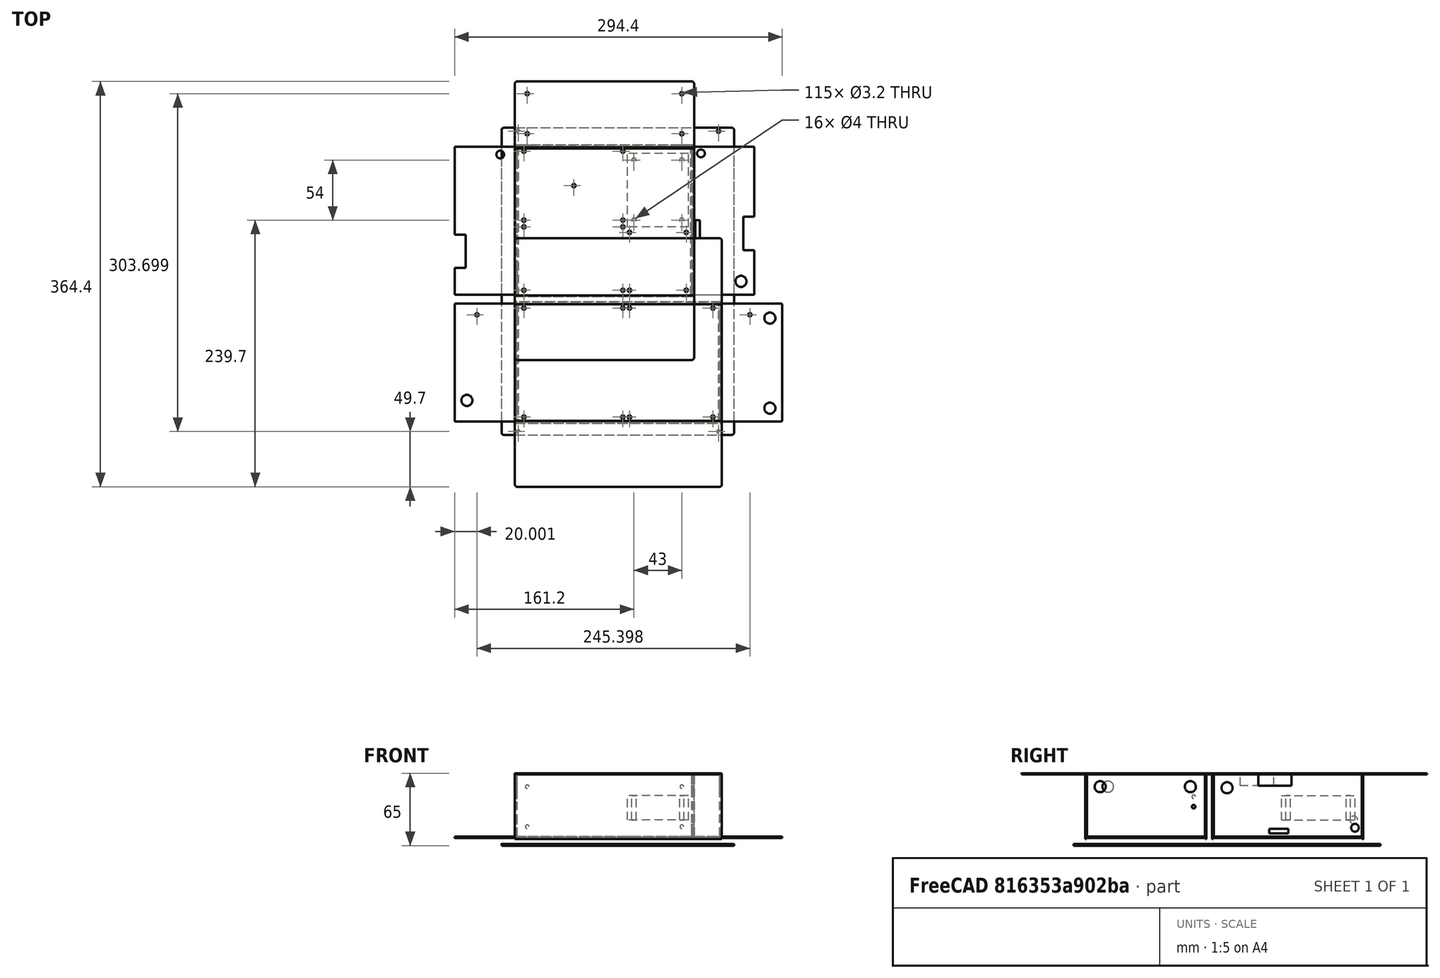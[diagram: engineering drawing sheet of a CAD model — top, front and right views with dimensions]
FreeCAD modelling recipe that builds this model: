
FCSTD DOCUMENT  (FreeCAD 0.19R24267 +99 (Git))
Label: inth_1
License: All rights reserved
LicenseURL: http://en.wikipedia.org/wiki/All_rights_reserved
objects: Part::Cylinder×91, TechDraw::DrawViewDimension×33, TechDraw::DrawViewPart×17, Sketcher::SketchObject×10, Part::MultiFuse×10, Part::Cut×10, Part::FeaturePython×8, TechDraw::DrawSVGTemplate×8, TechDraw::DrawPage×8, Part::Box×5, Part::Fillet×5, TechDraw::DrawViewAnnotation×5, Part::Extrusion×4, Part::Feature×4, PartDesign::Body×1
note: 148 computed .brp shape members not serialized (recipe doc carries the construction recipe); baked Part::Feature solids carry a one-line shape summary decoded from their .brp

FEATURE [Sketcher::SketchObject] Sketch001
  FullyConstrained = true
  MapMode = 5
  sketch-geometry (4):
    g0: LineSegment StartX=0 StartY=0 StartZ=0 EndX=180 EndY=0 EndZ=0
    g1: LineSegment StartX=180 StartY=0 StartZ=0 EndX=180 EndY=106 EndZ=0
    g2: LineSegment StartX=180 StartY=106 StartZ=0 EndX=0 EndY=106 EndZ=0
    g3: LineSegment StartX=0 StartY=106 StartZ=0 EndX=0 EndY=0 EndZ=0
  constraints (11):
    c: Coincident(g0,g1)
    c: Coincident(g1,g2)
    c: Coincident(g2,g3)
    c: Coincident(g3,g0)
    c: Horizontal(g0)
    c: Horizontal(g2)
    c: Vertical(g1)
    c: Vertical(g3)
    c: Coincident(g0,g-1)
    c: DistanceX(g2,g2) = 180
    c: DistanceY(g1,g1) = 106
FEATURE [Part::Extrusion] Extrude001
  Base = -> Sketch001
  Dir = (0,0,1)
  DirMode = 2
  FaceMakerClass = Part::FaceMakerBullseye
  LengthFwd = 1
  LengthRev = 0
  Placement = pos=(0,2,0) rot=(0,0,1;0rad)
  Solid = true
  Symmetric = false
FEATURE [Sketcher::SketchObject] Sketch004
  FullyConstrained = true
  MapMode = 5
  Support = -> [XY_Plane]
  sketch-geometry (4):
    g0: LineSegment StartX=0 StartY=114 StartZ=0 EndX=161 EndY=114 EndZ=0
    g1: LineSegment StartX=161 StartY=114 StartZ=0 EndX=161 EndY=246 EndZ=0
    g2: LineSegment StartX=161 StartY=246 StartZ=0 EndX=0 EndY=246 EndZ=0
    g3: LineSegment StartX=0 StartY=246 StartZ=0 EndX=0 EndY=114 EndZ=0
  constraints (12):
    c: Coincident(g0,g1)
    c: Coincident(g1,g2)
    c: Coincident(g2,g3)
    c: Coincident(g3,g0)
    c: Horizontal(g0)
    c: Horizontal(g2)
    c: Vertical(g1)
    c: Vertical(g3)
    c: PointOnObject(g0,g-2)
    c: DistanceY(g-1,g0) = 114
    c: DistanceY(g3,g3) = 132
    c: DistanceX(g2,g2) = 161
FEATURE [Part::Extrusion] Extrude003
  Base = -> Sketch004
  Dir = (0,0,1)
  DirMode = 2
  FaceMakerClass = Part::FaceMakerBullseye
  LengthFwd = 1
  LengthRev = 0
  Placement = pos=(-3,1.5,57) rot=(0,0,1;0rad)
  Solid = true
  Symmetric = false
FEATURE [Part::Cylinder] Cylinder
  Angle = 360
  AttacherType = Attacher::AttachEngine3D
  Height = 10
  Placement = pos=(5,6,0) rot=(0,0,1;0rad)
  Radius = 1.6
FEATURE [Part::Cylinder] Cylinder001
  Angle = 360
  AttacherType = Attacher::AttachEngine3D
  Height = 10
  Placement = pos=(5,104,0) rot=(0,0,1;0rad)
  Radius = 1.6
FEATURE [Part::Cylinder] Cylinder002
  Angle = 360
  AttacherType = Attacher::AttachEngine3D
  Height = 10
  Placement = pos=(94,104,0) rot=(0,0,1;0rad)
  Radius = 1.6
FEATURE [Part::Cylinder] Cylinder003
  Angle = 360
  AttacherType = Attacher::AttachEngine3D
  Height = 10
  Placement = pos=(94,6,0) rot=(0,0,1;0rad)
  Radius = 1.6
FEATURE [Part::Cylinder] Cylinder004
  Angle = 360
  AttacherType = Attacher::AttachEngine3D
  Height = 10
  Placement = pos=(100,6,0) rot=(0,0,1;0rad)
  Radius = 1.6
FEATURE [Part::Cylinder] Cylinder005
  Angle = 360
  AttacherType = Attacher::AttachEngine3D
  Height = 10
  Placement = pos=(100,104,0) rot=(0,0,1;0rad)
  Radius = 1.6
FEATURE [Part::Cylinder] Cylinder006
  Angle = 360
  AttacherType = Attacher::AttachEngine3D
  Height = 10
  Placement = pos=(175,6,0) rot=(0,0,1;0rad)
  Radius = 1.6
FEATURE [Part::Cylinder] Cylinder007
  Angle = 360
  AttacherType = Attacher::AttachEngine3D
  Height = 10
  Placement = pos=(175,104,0) rot=(0,0,1;0rad)
  Radius = 1.6
FEATURE [Part::Cylinder] Cylinder008
  Angle = 360
  AttacherType = Attacher::AttachEngine3D
  Height = 10
  Placement = pos=(5,120,0) rot=(0,0,1;0rad)
  Radius = 1.6
FEATURE [Part::Cylinder] Cylinder009
  Angle = 360
  AttacherType = Attacher::AttachEngine3D
  Height = 10
  Placement = pos=(5,245,0) rot=(0,0,1;0rad)
  Radius = 1.6
FEATURE [Part::Box] Box  label="Cube"
  AttacherType = Attacher::AttachEngine3D
  Height = 22
  Length = 66
  Width = 55
FEATURE [Part::Cylinder] Cylinder010
  Angle = 360
  AttacherType = Attacher::AttachEngine3D
  Height = 30
  Placement = pos=(6,6,0) rot=(0,0,1;0rad)
  Radius = 2
FEATURE [Part::Cylinder] Cylinder011
  Angle = 360
  AttacherType = Attacher::AttachEngine3D
  Height = 30
  Placement = pos=(60,49,0) rot=(0,0,1;0rad)
  Radius = 2
FEATURE [Part::Cylinder] Cylinder012
  Angle = 360
  AttacherType = Attacher::AttachEngine3D
  Height = 30
  Placement = pos=(6,49,0) rot=(0,0,1;0rad)
  Radius = 2
FEATURE [Part::Cylinder] Cylinder013
  Angle = 360
  AttacherType = Attacher::AttachEngine3D
  Height = 30
  Placement = pos=(60,6,0) rot=(0,0,1;0rad)
  Radius = 2
FEATURE [Part::MultiFuse] Fusion
  Shapes = -> [Cylinder010,Cylinder011,Cylinder012,Cylinder013]
FEATURE [Part::Cut] Cut
  Base = -> Box
  Placement = pos=(153,177,16) rot=(0,0,1;1.5708rad)
  Tool = -> Fusion
FEATURE [Part::Cylinder] Cylinder014
  Angle = 360
  AttacherType = Attacher::AttachEngine3D
  Height = 10
  Placement = pos=(94,245,0) rot=(0,0,1;0rad)
  Radius = 1.6
FEATURE [Part::Cylinder] Cylinder015
  Angle = 360
  AttacherType = Attacher::AttachEngine3D
  Height = 10
  Placement = pos=(94,183,0) rot=(0,0,1;0rad)
  Radius = 1.6
FEATURE [Part::Cylinder] Cylinder016
  Angle = 360
  AttacherType = Attacher::AttachEngine3D
  Height = 10
  Placement = pos=(5,183,0) rot=(0,0,1;0rad)
  Radius = 1.6
FEATURE [Part::Cylinder] Cylinder017
  Angle = 360
  AttacherType = Attacher::AttachEngine3D
  Height = 10
  Placement = pos=(5,177,0) rot=(0,0,1;0rad)
  Radius = 1.6
FEATURE [Part::Cylinder] Cylinder018
  Angle = 360
  AttacherType = Attacher::AttachEngine3D
  Height = 10
  Placement = pos=(94,177,0) rot=(0,0,1;0rad)
  Radius = 1.6
FEATURE [Part::Cylinder] Cylinder019
  Angle = 360
  AttacherType = Attacher::AttachEngine3D
  Height = 10
  Placement = pos=(94,120,0) rot=(0,0,1;0rad)
  Radius = 1.6
FEATURE [Part::Cylinder] Cylinder020
  Angle = 360
  AttacherType = Attacher::AttachEngine3D
  Height = 10
  Placement = pos=(100,120,0) rot=(0,0,1;0rad)
  Radius = 1.6
FEATURE [Part::Cylinder] Cylinder021
  Angle = 360
  AttacherType = Attacher::AttachEngine3D
  Height = 10
  Placement = pos=(100,172,0) rot=(0,0,1;0rad)
  Radius = 1.6
FEATURE [Part::Cylinder] Cylinder022
  Angle = 360
  AttacherType = Attacher::AttachEngine3D
  Height = 10
  Placement = pos=(151,172,0) rot=(0,0,1;0rad)
  Radius = 1.6
FEATURE [Part::Cylinder] Cylinder023
  Angle = 360
  AttacherType = Attacher::AttachEngine3D
  Height = 10
  Placement = pos=(151,120,0) rot=(0,0,1;0rad)
  Radius = 1.6
FEATURE [Part::Cylinder] Cylinder024
  Angle = 360
  AttacherType = Attacher::AttachEngine3D
  Height = 10
  Placement = pos=(50,214,0) rot=(0,0,1;0rad)
  Radius = 1.6
FEATURE [Part::Cylinder] Cylinder025
  Angle = 360
  AttacherType = Attacher::AttachEngine3D
  Height = 10
  Placement = pos=(147,183,0) rot=(0,0,1;0rad)
  Radius = 2
FEATURE [Part::Cylinder] Cylinder026
  Angle = 360
  AttacherType = Attacher::AttachEngine3D
  Height = 10
  Placement = pos=(104,183,0) rot=(0,0,1;0rad)
  Radius = 2
FEATURE [Part::Cylinder] Cylinder027
  Angle = 360
  AttacherType = Attacher::AttachEngine3D
  Height = 10
  Placement = pos=(104,237,0) rot=(0,0,1;0rad)
  Radius = 2
FEATURE [Part::Cylinder] Cylinder028
  Angle = 360
  AttacherType = Attacher::AttachEngine3D
  Height = 10
  Placement = pos=(147,237,0) rot=(0,0,1;0rad)
  Radius = 2
FEATURE [Part::Box] Box001  label="Cube001"
  AttacherType = Attacher::AttachEngine3D
  Height = 1.5
  Length = 209
  Placement = pos=(-15,-10,0) rot=(0,0,1;0rad)
  Width = 276
FEATURE [Part::Cylinder] Cylinder029
  Angle = 360
  AttacherType = Attacher::AttachEngine3D
  Height = 10
  Placement = pos=(0,-7,0) rot=(0,0,1;0rad)
  Radius = 1.6
FEATURE [Part::Cylinder] Cylinder030
  Angle = 360
  AttacherType = Attacher::AttachEngine3D
  Height = 10
  Placement = pos=(180,-7,0) rot=(0,0,1;0rad)
  Radius = 1.6
FEATURE [Part::Cylinder] Cylinder031
  Angle = 360
  AttacherType = Attacher::AttachEngine3D
  Height = 10
  Placement = pos=(0,263,0) rot=(0,0,1;0rad)
  Radius = 1.6
FEATURE [Part::Cylinder] Cylinder032
  Angle = 360
  AttacherType = Attacher::AttachEngine3D
  Height = 10
  Placement = pos=(180,263,0) rot=(0,0,1;0rad)
  Radius = 1.6
FEATURE [Sketcher::SketchObject] Sketch003
  FullyConstrained = true
  MapMode = 5
  Support = -> [XY_Plane]
  sketch-geometry (4):
    g0: LineSegment StartX=0 StartY=116 StartZ=0 EndX=155 EndY=116 EndZ=0
    g1: LineSegment StartX=155 StartY=116 StartZ=0 EndX=155 EndY=249 EndZ=0
    g2: LineSegment StartX=155 StartY=249 StartZ=0 EndX=0 EndY=249 EndZ=0
    g3: LineSegment StartX=0 StartY=249 StartZ=0 EndX=0 EndY=116 EndZ=0
  constraints (12):
    c: Coincident(g0,g1)
    c: Coincident(g1,g2)
    c: Coincident(g2,g3)
    c: Coincident(g3,g0)
    c: Horizontal(g0)
    c: Horizontal(g2)
    c: Vertical(g1)
    c: Vertical(g3)
    c: PointOnObject(g0,g-2)
    c: DistanceY(g-1,g0) = 116
    c: DistanceY(g3,g3) = 133
    c: DistanceX(g2,g2) = 155
FEATURE [Part::Extrusion] Extrude002
  Base = -> Sketch003
  Dir = (0,0,1)
  DirMode = 2
  FaceMakerClass = Part::FaceMakerBullseye
  LengthFwd = 1
  LengthRev = 0
  Solid = true
  Symmetric = false
FEATURE [Sketcher::SketchObject] Sketch005
  FullyConstrained = true
  MapMode = 5
  Support = -> [XY_Plane]
  sketch-geometry (4):
    g0: LineSegment StartX=-15 StartY=-10 StartZ=0 EndX=195 EndY=-10 EndZ=0
    g1: LineSegment StartX=195 StartY=-10 StartZ=0 EndX=195 EndY=266 EndZ=0
    g2: LineSegment StartX=195 StartY=266 StartZ=0 EndX=-15 EndY=266 EndZ=0
    g3: LineSegment StartX=-15 StartY=266 StartZ=0 EndX=-15 EndY=-10 EndZ=0
  constraints (12):
    c: Coincident(g0,g1)
    c: Coincident(g1,g2)
    c: Coincident(g2,g3)
    c: Coincident(g3,g0)
    c: Horizontal(g0)
    c: Horizontal(g2)
    c: Vertical(g1)
    c: Vertical(g3)
    c: DistanceY(g1,g1) = 276
    c: DistanceX(g2,g2) = 210
    c: DistanceY(g0,g-1) = 10
    c: DistanceX(g0,g-1) = 15
FEATURE [Sketcher::SketchObject] Sketch006
  FullyConstrained = false
  MapMode = 5
  Placement = pos=(0,0,1.5) rot=(0,0,1;0rad)
  sketch-geometry (4):
    g0: Circle CenterX=0 CenterY=-7 CenterZ=0 NormalX=0 NormalY=0 NormalZ=1 AngleXU=0 Radius=1.6
    g1: Circle CenterX=180 CenterY=-7 CenterZ=0 NormalX=0 NormalY=0 NormalZ=1 AngleXU=0 Radius=1.6
    g2: Circle CenterX=-8.83118 CenterY=263 CenterZ=0 NormalX=0 NormalY=0 NormalZ=1 AngleXU=0 Radius=1.6
    g3: Circle CenterX=171.169 CenterY=263 CenterZ=0 NormalX=0 NormalY=0 NormalZ=1 AngleXU=0 Radius=1.6
  constraints (11):
    c: Diameter(g3) = 3.2
    c: DistanceX(g2,g3) = 180
    c: Diameter(g2) = 3.2
    c: Diameter(g0) = 3.2
    c: Diameter(g1) = 3.2
    c: DistanceX(g0,g1) = 180
    c: DistanceY(g0,g2) = 270
    c: DistanceY(g0,g-1) = 7
    c: DistanceX(g-1,g0) = 0
    c: DistanceY(g2,g3) = 0
    c: DistanceY(g0,g1) = 0
FEATURE [Part::Cylinder] Cylinder033
  Angle = 360
  AttacherType = Attacher::AttachEngine3D
  Height = 10
  Placement = pos=(94,104,0) rot=(0,0,1;0rad)
  Radius = 1.6
FEATURE [Part::Cylinder] Cylinder034
  Angle = 360
  AttacherType = Attacher::AttachEngine3D
  Height = 10
  Placement = pos=(5,104,0) rot=(0,0,1;0rad)
  Radius = 1.6
FEATURE [Part::Cylinder] Cylinder035
  Angle = 360
  AttacherType = Attacher::AttachEngine3D
  Height = 10
  Placement = pos=(5,120,0) rot=(0,0,1;0rad)
  Radius = 1.6
FEATURE [Part::Cylinder] Cylinder036
  Angle = 360
  AttacherType = Attacher::AttachEngine3D
  Height = 10
  Placement = pos=(5,177,0) rot=(0,0,1;0rad)
  Radius = 1.6
FEATURE [Part::Cylinder] Cylinder037
  Angle = 360
  AttacherType = Attacher::AttachEngine3D
  Height = 10
  Placement = pos=(94,120,0) rot=(0,0,1;0rad)
  Radius = 1.6
FEATURE [Part::Cylinder] Cylinder038
  Angle = 360
  AttacherType = Attacher::AttachEngine3D
  Height = 10
  Placement = pos=(5,183,0) rot=(0,0,1;0rad)
  Radius = 1.6
FEATURE [Part::Cylinder] Cylinder039
  Angle = 360
  AttacherType = Attacher::AttachEngine3D
  Height = 10
  Placement = pos=(94,177,0) rot=(0,0,1;0rad)
  Radius = 1.6
FEATURE [Part::Cylinder] Cylinder040
  Angle = 360
  AttacherType = Attacher::AttachEngine3D
  Height = 10
  Placement = pos=(5,6,0) rot=(0,0,1;0rad)
  Radius = 1.6
FEATURE [Part::Cylinder] Cylinder041
  Angle = 360
  AttacherType = Attacher::AttachEngine3D
  Height = 10
  Placement = pos=(50,214,0) rot=(0,0,1;0rad)
  Radius = 1.6
FEATURE [Part::Cylinder] Cylinder042
  Angle = 360
  AttacherType = Attacher::AttachEngine3D
  Height = 10
  Placement = pos=(175,104,0) rot=(0,0,1;0rad)
  Radius = 1.6
FEATURE [Part::Cylinder] Cylinder043
  Angle = 360
  AttacherType = Attacher::AttachEngine3D
  Height = 10
  Placement = pos=(94,245,0) rot=(0,0,1;0rad)
  Radius = 1.6
FEATURE [Part::Cylinder] Cylinder044
  Angle = 360
  AttacherType = Attacher::AttachEngine3D
  Height = 10
  Placement = pos=(175,6,0) rot=(0,0,1;0rad)
  Radius = 1.6
FEATURE [Part::Cylinder] Cylinder045
  Angle = 360
  AttacherType = Attacher::AttachEngine3D
  Height = 10
  Placement = pos=(100,104,0) rot=(0,0,1;0rad)
  Radius = 1.6
FEATURE [Part::Cylinder] Cylinder046
  Angle = 360
  AttacherType = Attacher::AttachEngine3D
  Height = 10
  Placement = pos=(5,245,0) rot=(0,0,1;0rad)
  Radius = 1.6
FEATURE [Part::Cylinder] Cylinder047
  Angle = 360
  AttacherType = Attacher::AttachEngine3D
  Height = 10
  Placement = pos=(94,6,0) rot=(0,0,1;0rad)
  Radius = 1.6
FEATURE [Part::Cylinder] Cylinder052
  Angle = 360
  AttacherType = Attacher::AttachEngine3D
  Height = 10
  Placement = pos=(100,6,0) rot=(0,0,1;0rad)
  Radius = 1.6
FEATURE [Part::Cylinder] Cylinder053
  Angle = 360
  AttacherType = Attacher::AttachEngine3D
  Height = 10
  Placement = pos=(151,172,0) rot=(0,0,1;0rad)
  Radius = 1.6
FEATURE [Part::Cylinder] Cylinder054
  Angle = 360
  AttacherType = Attacher::AttachEngine3D
  Height = 10
  Placement = pos=(151,120,0) rot=(0,0,1;0rad)
  Radius = 1.6
FEATURE [Part::Cylinder] Cylinder055
  Angle = 360
  AttacherType = Attacher::AttachEngine3D
  Height = 10
  Placement = pos=(94,183,0) rot=(0,0,1;0rad)
  Radius = 1.6
FEATURE [Part::Cylinder] Cylinder056
  Angle = 360
  AttacherType = Attacher::AttachEngine3D
  Height = 10
  Placement = pos=(147,237,0) rot=(0,0,1;0rad)
  Radius = 2
FEATURE [Part::Cylinder] Cylinder057
  Angle = 360
  AttacherType = Attacher::AttachEngine3D
  Height = 10
  Placement = pos=(104,237,0) rot=(0,0,1;0rad)
  Radius = 2
FEATURE [Part::Cylinder] Cylinder058
  Angle = 360
  AttacherType = Attacher::AttachEngine3D
  Height = 10
  Placement = pos=(147,183,0) rot=(0,0,1;0rad)
  Radius = 2
FEATURE [Part::Cylinder] Cylinder059
  Angle = 360
  AttacherType = Attacher::AttachEngine3D
  Height = 10
  Placement = pos=(104,183,0) rot=(0,0,1;0rad)
  Radius = 2
FEATURE [Part::Cylinder] Cylinder060
  Angle = 360
  AttacherType = Attacher::AttachEngine3D
  Height = 10
  Placement = pos=(100,172,0) rot=(0,0,1;0rad)
  Radius = 1.6
FEATURE [Part::Cylinder] Cylinder061
  Angle = 360
  AttacherType = Attacher::AttachEngine3D
  Height = 10
  Placement = pos=(100,120,0) rot=(0,0,1;0rad)
  Radius = 1.6
FEATURE [Part::MultiFuse] Fusion002
  Placement = pos=(0,0,-3) rot=(0,0,1;0rad)
  Shapes = -> [Cylinder033,Cylinder034,Cylinder040,Cylinder042,Cylinder044,Cylinder045,Cylinder047,Cylinder052]
FEATURE [Part::FeaturePython] Bend008  # WARN: FeaturePython — macro-defined, semantics opaque (R4)
  AutoMiter = true
  BendType = 0
  LengthList = [55]
  ReliefFactor = 0.7
  UseReliefFactor = false
  angle = 90
  baseObject = -> Extrude001 [Face4]
  bendAList = [90]
  extend1 = 0
  extend2 = 0
  gap1 = 0
  gap2 = 0
  invert = false
  kfactor = 0.5
  length = 55
  maxExtendDist = 5
  minGap = 0.1
  minReliefGap = 1
  miterangle1 = 0
  miterangle2 = 0
  offset = 0
  radius = 1
  reliefType = 0
  reliefd = 1
  reliefw = 0.8
  sketchflip = false
  sketchinvert = false
  unfold = false
FEATURE [Part::FeaturePython] Bend009  # WARN: FeaturePython — macro-defined, semantics opaque (R4)
  AutoMiter = true
  BendType = 0
  LengthList = [55]
  ReliefFactor = 0.7
  UseReliefFactor = false
  angle = 90
  baseObject = -> Bend008 [Face13]
  bendAList = [90]
  extend1 = 0
  extend2 = 0
  gap1 = 0
  gap2 = 0
  invert = false
  kfactor = 0.5
  length = 55
  maxExtendDist = 5
  minGap = 0.1
  minReliefGap = 1
  miterangle1 = 0
  miterangle2 = 0
  offset = 0
  radius = 1
  reliefType = 0
  reliefd = 1
  reliefw = 0.8
  sketchflip = false
  sketchinvert = false
  unfold = false
FEATURE [Part::FeaturePython] Bend010  # WARN: FeaturePython — macro-defined, semantics opaque (R4)
  AutoMiter = true
  BendType = 0
  LengthList = [55]
  ReliefFactor = 0.7
  UseReliefFactor = false
  angle = 90
  baseObject = -> Extrude002 [Face2]
  bendAList = [90]
  extend1 = 0
  extend2 = 0
  gap1 = 0
  gap2 = 0
  invert = false
  kfactor = 0.5
  length = 55
  maxExtendDist = 5
  minGap = 0.1
  minReliefGap = 1
  miterangle1 = 0
  miterangle2 = 0
  offset = 0
  radius = 1
  reliefType = 0
  reliefd = 1
  reliefw = 0.8
  sketchflip = false
  sketchinvert = false
  unfold = false
FEATURE [Part::FeaturePython] Bend011  # WARN: FeaturePython — macro-defined, semantics opaque (R4)
  AutoMiter = true
  BendType = 0
  LengthList = [55]
  ReliefFactor = 0.7
  UseReliefFactor = false
  angle = 90
  baseObject = -> Bend010 [Face13]
  bendAList = [90]
  extend1 = 0
  extend2 = 0
  gap1 = 0
  gap2 = 0
  invert = false
  kfactor = 0.5
  length = 55
  maxExtendDist = 5
  minGap = 0.1
  minReliefGap = 1
  miterangle1 = 0
  miterangle2 = 0
  offset = 0
  radius = 1
  reliefType = 0
  reliefd = 1
  reliefw = 0.8
  sketchflip = false
  sketchinvert = false
  unfold = false
FEATURE [Part::FeaturePython] Bend  # WARN: FeaturePython — macro-defined, semantics opaque (R4)
  AutoMiter = true
  BendType = 0
  LengthList = [57]
  Placement = pos=(0,1,0) rot=(0,0,1;0rad)
  ReliefFactor = 0.7
  UseReliefFactor = false
  angle = 90
  baseObject = -> Extrude003 [Face1]
  bendAList = [90]
  extend1 = 0
  extend2 = 0
  gap1 = 0
  gap2 = 0
  invert = true
  kfactor = 0.5
  length = 57
  maxExtendDist = 5
  minGap = 0.1
  minReliefGap = 1
  miterangle1 = 0
  miterangle2 = 0
  offset = 0
  radius = 1
  reliefType = 0
  reliefd = 1
  reliefw = 0.8
  sketchflip = false
  sketchinvert = false
  unfold = false
FEATURE [Part::FeaturePython] Bend012  # WARN: FeaturePython — macro-defined, semantics opaque (R4)
  AutoMiter = true
  BendType = 0
  LengthList = [57]
  ReliefFactor = 0.7
  UseReliefFactor = false
  angle = 90
  baseObject = -> Bend [Face13]
  bendAList = [90]
  extend1 = 0
  extend2 = 0
  gap1 = 0
  gap2 = 0
  invert = true
  kfactor = 0.5
  length = 57
  maxExtendDist = 5
  minGap = 0.1
  minReliefGap = 1
  miterangle1 = 0
  miterangle2 = 0
  offset = 0
  radius = 1
  reliefType = 0
  reliefd = 1
  reliefw = 0.8
  sketchflip = false
  sketchinvert = false
  unfold = false
FEATURE [Sketcher::SketchObject] Sketch
  FullyConstrained = true
  MapMode = 5
  Support = -> [XY_Plane]
  sketch-geometry (4):
    g0: LineSegment StartX=0 StartY=0 StartZ=0 EndX=186 EndY=0 EndZ=0
    g1: LineSegment StartX=186 StartY=0 StartZ=0 EndX=186 EndY=105 EndZ=0
    g2: LineSegment StartX=186 StartY=105 StartZ=0 EndX=0 EndY=105 EndZ=0
    g3: LineSegment StartX=0 StartY=105 StartZ=0 EndX=0 EndY=0 EndZ=0
  constraints (11):
    c: Coincident(g0,g1)
    c: Coincident(g1,g2)
    c: Coincident(g2,g3)
    c: Coincident(g3,g0)
    c: Horizontal(g0)
    c: Horizontal(g2)
    c: Vertical(g1)
    c: Vertical(g3)
    c: Coincident(g0,g-1)
    c: DistanceX(g2,g2) = 186
    c: DistanceY(g1,g1) = 105
FEATURE [PartDesign::Body] Body
  Group = -> [Sketch,Sketch003,Sketch005,Sketch006]
  Origin = -> Origin
  Placement = pos=(0,0,-5) rot=(0,0,1;0rad)
FEATURE [Part::Extrusion] Extrude
  Base = -> Sketch
  Dir = (0,0,1)
  DirMode = 2
  FaceMakerClass = Part::FaceMakerBullseye
  LengthFwd = 1
  LengthRev = 0
  Placement = pos=(-3,2.5,57) rot=(-0.894427,0,0.447214;0rad)
  Solid = true
  Symmetric = false
FEATURE [Part::FeaturePython] Bend013  # WARN: FeaturePython — macro-defined, semantics opaque (R4)
  AutoMiter = true
  BendType = 0
  LengthList = [57]
  ReliefFactor = 0.7
  UseReliefFactor = false
  angle = 90
  baseObject = -> Extrude [Face3]
  bendAList = [90]
  extend1 = 0
  extend2 = 0
  gap1 = 0
  gap2 = 0
  invert = true
  kfactor = 0.5
  length = 57
  maxExtendDist = 5
  minGap = 0.1
  minReliefGap = 1
  miterangle1 = 0
  miterangle2 = 0
  offset = 0
  radius = 1
  reliefType = 0
  reliefd = 1
  reliefw = 0.8
  sketchflip = false
  sketchinvert = false
  unfold = false
FEATURE [Part::FeaturePython] Bend014  # WARN: FeaturePython — macro-defined, semantics opaque (R4)
  AutoMiter = true
  BendType = 0
  LengthList = [57]
  ReliefFactor = 0.7
  UseReliefFactor = false
  angle = 90
  baseObject = -> Bend013 [Face13]
  bendAList = [90]
  extend1 = 0
  extend2 = 0
  gap1 = 0
  gap2 = 0
  invert = true
  kfactor = 0.5
  length = 57
  maxExtendDist = 5
  minGap = 0.1
  minReliefGap = 1
  miterangle1 = 0
  miterangle2 = 0
  offset = 0
  radius = 1
  reliefType = 0
  reliefd = 1
  reliefw = 0.8
  sketchflip = false
  sketchinvert = false
  unfold = false
FEATURE [Part::Fillet] Fillet
  Base = -> Bend009
  Edges = 4 edges r=1: [Edge2,Edge8,Edge36,Edge44]
FEATURE [Part::Fillet] Fillet001
  Base = -> Bend011
  Edges = 4 edges r=1: [Edge2,Edge8,Edge36,Edge44]
FEATURE [Part::Cylinder] Cylinder062
  Angle = 360
  AttacherType = Attacher::AttachEngine3D
  Height = 10
  Placement = pos=(-8,21,46) rot=(0,1,0;1.5708rad)
  Radius = 5
FEATURE [Part::Cut] Cut003
  Base = -> Fillet
  Tool = -> Fusion002
FEATURE [Part::Cylinder] Cylinder063
  Angle = 360
  AttacherType = Attacher::AttachEngine3D
  Height = 10
  Placement = pos=(176,95,46) rot=(0,1,0;1.5708rad)
  Radius = 5
FEATURE [Part::MultiFuse] Fusion004
  Shapes = -> [Cylinder063,Cylinder062]
FEATURE [Part::Cut] Cut004
  Base = -> Cut003
  Tool = -> Fusion004
FEATURE [Part::MultiFuse] Fusion005
  Shapes = -> [Cylinder035,Cylinder036,Cylinder037,Cylinder038,Cylinder039,Cylinder041,Cylinder043,Cylinder046,Cylinder053,Cylinder054,Cylinder055,Cylinder056,Cylinder057,Cylinder058,Cylinder059,Cylinder060,Cylinder061]
FEATURE [Part::Cut] Cut005
  Base = -> Fillet001
  Tool = -> Fusion005
FEATURE [Part::MultiFuse] Fusion006
  Shapes = -> [Cylinder,Cylinder001,Cylinder002,Cylinder003,Cylinder004,Cylinder005,Cylinder006,Cylinder007,Cylinder008,Cylinder009,Cylinder014,Cylinder015,Cylinder016,Cylinder017,Cylinder018,Cylinder019,Cylinder020,Cylinder021,Cylinder022,Cylinder023,Cylinder024,Cylinder025,Cylinder026,Cylinder027,Cylinder028,Cylinder029,Cylinder030,Cylinder031,Cylinder032]
FEATURE [Part::Cut] Cut006
  Base = -> Box001
  Placement = pos=(0,0,-7) rot=(0,0,1;0rad)
  Tool = -> Fusion006
FEATURE [Part::Cylinder] Cylinder064
  Angle = 360
  AttacherType = Attacher::AttachEngine3D
  Height = 10
  Placement = pos=(152,243,9) rot=(0,1,0;1.5708rad)
  Radius = 3.5
FEATURE [Part::Cylinder] Cylinder065
  Angle = 360
  AttacherType = Attacher::AttachEngine3D
  Height = 10
  Placement = pos=(-5,242,16) rot=(0,1,0;1.5708rad)
  Radius = 3.5
FEATURE [Part::Cylinder] Cylinder066
  Angle = 360
  AttacherType = Attacher::AttachEngine3D
  Height = 10
  Placement = pos=(154,128,45) rot=(0,1,0;1.5708rad)
  Radius = 5
FEATURE [Part::Box] Box002  label="Cube002"
  AttacherType = Attacher::AttachEngine3D
  Height = 10
  Length = 10
  Placement = pos=(-8,140,47) rot=(0,0,1;0rad)
  Width = 30
FEATURE [Part::Box] Box003  label="Cube003"
  AttacherType = Attacher::AttachEngine3D
  Height = 10
  Length = 10
  Placement = pos=(149,156,47) rot=(0,0,1;0rad)
  Width = 30
FEATURE [Part::Box] Box004  label="Cube004"
  AttacherType = Attacher::AttachEngine3D
  Height = 4
  Length = 10
  Placement = pos=(151,166,4) rot=(0,0,1;0rad)
  Width = 17
FEATURE [Part::MultiFuse] Fusion007
  Shapes = -> [Cylinder065,Box002,Cylinder064,Box004,Box003,Cylinder066]
FEATURE [Part::Cut] Cut007
  Base = -> Cut005
  Tool = -> Fusion007
FEATURE [Part::Fillet] Fillet002
  Base = -> Bend012
  Edges = 4 edges r=2: [Edge2,Edge8,Edge36,Edge44]
FEATURE [Part::Fillet] Fillet003
  Base = -> Bend014
  Edges = 4 edges r=2: [Edge2,Edge8,Edge36,Edge44]
FEATURE [Part::Fillet] Fillet004
  Base = -> Cut006
  Edges = 4 edges r=2: [Edge1,Edge3,Edge6,Edge40]
FEATURE [Part::Cylinder] Cylinder067
  Angle = 360
  AttacherType = Attacher::AttachEngine3D
  Height = 10
  Placement = pos=(5,120,0) rot=(0,0,1;0rad)
  Radius = 1.6
FEATURE [Part::Cylinder] Cylinder068
  Angle = 360
  AttacherType = Attacher::AttachEngine3D
  Height = 10
  Placement = pos=(5,177,0) rot=(0,0,1;0rad)
  Radius = 1.6
FEATURE [Part::Cylinder] Cylinder069
  Angle = 360
  AttacherType = Attacher::AttachEngine3D
  Height = 10
  Placement = pos=(94,120,0) rot=(0,0,1;0rad)
  Radius = 1.6
FEATURE [Part::Cylinder] Cylinder070
  Angle = 360
  AttacherType = Attacher::AttachEngine3D
  Height = 10
  Placement = pos=(5,183,0) rot=(0,0,1;0rad)
  Radius = 1.6
FEATURE [Part::Cylinder] Cylinder071
  Angle = 360
  AttacherType = Attacher::AttachEngine3D
  Height = 10
  Placement = pos=(94,177,0) rot=(0,0,1;0rad)
  Radius = 1.6
FEATURE [Part::Cylinder] Cylinder072
  Angle = 360
  AttacherType = Attacher::AttachEngine3D
  Height = 10
  Placement = pos=(50,214,0) rot=(0,0,1;0rad)
  Radius = 1.6
FEATURE [Part::Cylinder] Cylinder073
  Angle = 360
  AttacherType = Attacher::AttachEngine3D
  Height = 10
  Placement = pos=(94,245,0) rot=(0,0,1;0rad)
  Radius = 1.6
FEATURE [Part::Cylinder] Cylinder074
  Angle = 360
  AttacherType = Attacher::AttachEngine3D
  Height = 10
  Placement = pos=(5,245,0) rot=(0,0,1;0rad)
  Radius = 1.6
FEATURE [Part::Cylinder] Cylinder075
  Angle = 360
  AttacherType = Attacher::AttachEngine3D
  Height = 10
  Placement = pos=(151,172,0) rot=(0,0,1;0rad)
  Radius = 1.6
FEATURE [Part::Cylinder] Cylinder076
  Angle = 360
  AttacherType = Attacher::AttachEngine3D
  Height = 10
  Placement = pos=(151,120,0) rot=(0,0,1;0rad)
  Radius = 1.6
FEATURE [Part::Cylinder] Cylinder077
  Angle = 360
  AttacherType = Attacher::AttachEngine3D
  Height = 10
  Placement = pos=(94,183,0) rot=(0,0,1;0rad)
  Radius = 1.6
FEATURE [Part::Cylinder] Cylinder082
  Angle = 360
  AttacherType = Attacher::AttachEngine3D
  Height = 10
  Placement = pos=(100,172,0) rot=(0,0,1;0rad)
  Radius = 1.6
FEATURE [Part::Cylinder] Cylinder083
  Angle = 360
  AttacherType = Attacher::AttachEngine3D
  Height = 10
  Placement = pos=(100,120,0) rot=(0,0,1;0rad)
  Radius = 1.6
FEATURE [Part::MultiFuse] Fusion008
  Placement = pos=(0,0,54) rot=(0,0,1;0rad)
  Shapes = -> [Cylinder067,Cylinder068,Cylinder069,Cylinder070,Cylinder071,Cylinder072,Cylinder073,Cylinder074,Cylinder075,Cylinder076,Cylinder077,Cylinder082,Cylinder083]
FEATURE [Part::Cut] Cut008
  Base = -> Fillet002
  Tool = -> Fusion008
FEATURE [Part::Cylinder] Cylinder084
  Angle = 360
  AttacherType = Attacher::AttachEngine3D
  Height = 10
  Placement = pos=(94,104,0) rot=(0,0,1;0rad)
  Radius = 1.6
FEATURE [Part::Cylinder] Cylinder085
  Angle = 360
  AttacherType = Attacher::AttachEngine3D
  Height = 10
  Placement = pos=(5,104,0) rot=(0,0,1;0rad)
  Radius = 1.6
FEATURE [Part::Cylinder] Cylinder086
  Angle = 360
  AttacherType = Attacher::AttachEngine3D
  Height = 10
  Placement = pos=(5,6,0) rot=(0,0,1;0rad)
  Radius = 1.6
FEATURE [Part::Cylinder] Cylinder087
  Angle = 360
  AttacherType = Attacher::AttachEngine3D
  Height = 10
  Placement = pos=(175,104,0) rot=(0,0,1;0rad)
  Radius = 1.6
FEATURE [Part::Cylinder] Cylinder088
  Angle = 360
  AttacherType = Attacher::AttachEngine3D
  Height = 10
  Placement = pos=(175,6,0) rot=(0,0,1;0rad)
  Radius = 1.6
FEATURE [Part::Cylinder] Cylinder089
  Angle = 360
  AttacherType = Attacher::AttachEngine3D
  Height = 10
  Placement = pos=(100,104,0) rot=(0,0,1;0rad)
  Radius = 1.6
FEATURE [Part::Cylinder] Cylinder090
  Angle = 360
  AttacherType = Attacher::AttachEngine3D
  Height = 10
  Placement = pos=(94,6,0) rot=(0,0,1;0rad)
  Radius = 1.6
FEATURE [Part::Cylinder] Cylinder091
  Angle = 360
  AttacherType = Attacher::AttachEngine3D
  Height = 10
  Placement = pos=(100,6,0) rot=(0,0,1;0rad)
  Radius = 1.6
FEATURE [Part::MultiFuse] Fusion009
  Placement = pos=(0,0,51) rot=(0,0,1;0rad)
  Shapes = -> [Cylinder084,Cylinder085,Cylinder086,Cylinder087,Cylinder088,Cylinder089,Cylinder090,Cylinder091]
FEATURE [Part::Cut] Cut009
  Base = -> Fillet003
  Tool = -> Fusion009
FEATURE [Part::Cylinder] Cylinder092
  Angle = 360
  AttacherType = Attacher::AttachEngine3D
  Height = 10
  Placement = pos=(-6,98,37) rot=(0,1,0;1.5708rad)
  Radius = 1.6
FEATURE [Part::Cylinder] Cylinder093
  Angle = 360
  AttacherType = Attacher::AttachEngine3D
  Height = 10
  Placement = pos=(176,98,28) rot=(0,1,0;1.5708rad)
  Radius = 1.6
FEATURE [Part::Cylinder] Cylinder094
  Angle = 360
  AttacherType = Attacher::AttachEngine3D
  Height = 10
  Placement = pos=(176,14,46) rot=(0,1,0;1.5708rad)
  Radius = 5
FEATURE [Part::MultiFuse] Fusion010
  Shapes = -> [Cylinder094,Cylinder092,Cylinder093]
FEATURE [Part::Cut] Cut010
  Base = -> Cut004
  Tool = -> Fusion010
FEATURE [Part::Cylinder] Cylinder095
  Angle = 360
  AttacherType = Attacher::AttachEngine3D
  Height = 10
  Placement = pos=(147,255,46) rot=(1,0,0;1.5708rad)
  Radius = 1.6
FEATURE [Part::Cylinder] Cylinder096
  Angle = 360
  AttacherType = Attacher::AttachEngine3D
  Height = 10
  Placement = pos=(147,255,10) rot=(1,0,0;1.5708rad)
  Radius = 1.6
FEATURE [Part::Cylinder] Cylinder097
  Angle = 360
  AttacherType = Attacher::AttachEngine3D
  Height = 10
  Placement = pos=(8,255,46) rot=(1,0,0;1.5708rad)
  Radius = 1.6
FEATURE [Part::Cylinder] Cylinder098
  Angle = 360
  AttacherType = Attacher::AttachEngine3D
  Height = 10
  Placement = pos=(8,255,10) rot=(1,0,0;1.5708rad)
  Radius = 1.6
FEATURE [Part::MultiFuse] Fusion011
  Shapes = -> [Cylinder098,Cylinder095,Cylinder096,Cylinder097]
FEATURE [Part::Cut] Cut011
  Base = -> Cut008
  Tool = -> Fusion011
FEATURE [TechDraw::DrawSVGTemplate] Template
  EditableTexts = DATE=2021-12-18; DOCUMENT_TYPE=Mechanical assembly drawing; REVISION=REV A; RIGHTS=(R) DO NOT DUPLICATE THIS DRAWING TO THIRD PARTIES WITHOUT OWNER'S PERMISSION !; SCALE=M 0.5; SHEET=1; SIZE=A4; TITLELINE-1=NVM_BASE
  Height = 297
  Orientation = 0
  Width = 210
FEATURE [TechDraw::DrawViewPart] View
  CoarseView = false
  Direction = (0,0,1)
  Focus = 100
  HardHidden = false
  IsoCount = 0
  IsoHidden = false
  IsoVisible = false
  LockPosition = false
  Perspective = false
  Rotation = 0
  Scale = 0.5
  ScaleType = 2
  SeamHidden = false
  SeamVisible = true
  SmoothHidden = false
  SmoothVisible = true
  Source = -> [Fillet004]
  X = 105.458
  XDirection = (1,0,0)
  Y = 187.458
FEATURE [TechDraw::DrawViewDimension] Dimension
  Arbitrary = false
  ArbitraryTolerances = false
  EqualTolerance = true
  FormatSpec = %.2f
  FormatSpecOverTolerance = %+.2f
  FormatSpecUnderTolerance = %+.2f
  Inverted = false
  LockPosition = false
  MeasureType = 1
  OverTolerance = 0
  References2D = -> [View]
  Rotation = 0
  ScaleType = 0
  TheoreticalExact = false
  Type = 1
  UnderTolerance = 0
  X = -1.16768
  Y = 87.7337
FEATURE [TechDraw::DrawViewDimension] Dimension001
  Arbitrary = false
  ArbitraryTolerances = false
  EqualTolerance = true
  FormatSpec = %.2f
  FormatSpecOverTolerance = %+.2f
  FormatSpecUnderTolerance = %+.2f
  Inverted = false
  LockPosition = false
  MeasureType = 1
  OverTolerance = 0
  References2D = -> [View]
  Rotation = 0
  ScaleType = 0
  TheoreticalExact = false
  Type = 2
  UnderTolerance = 0
  X = -69.1676
  Y = -0.726387
FEATURE [Part::Feature] Unfold
  shape: bbox 269.4 x 133 x 1 mm, 42 faces (baked)
FEATURE [Sketcher::SketchObject] Unfold_Sketch
  FullyConstrained = false
  sketch-geometry (42):
    g0: ArcOfCircle CenterX=211.199 CenterY=248 CenterZ=0 NormalX=0 NormalY=0 NormalZ=1 AngleXU=-3.14159 Radius=1 StartAngle=3.14159 EndAngle=4.71239
    g1: LineSegment StartX=212.199 StartY=186 StartZ=0 EndX=212.199 EndY=248 EndZ=0
    g2: LineSegment StartX=212.199 StartY=186 StartZ=0 EndX=202.199 EndY=186 EndZ=0
    g3: LineSegment StartX=202.199 StartY=156 StartZ=0 EndX=202.199 EndY=186 EndZ=0
    g4: LineSegment StartX=212.199 StartY=156 StartZ=0 EndX=202.199 EndY=156 EndZ=0
    g5: LineSegment StartX=212.199 StartY=117 StartZ=0 EndX=212.199 EndY=156 EndZ=0
    g6: ArcOfCircle CenterX=211.199 CenterY=117 CenterZ=0 NormalX=0 NormalY=0 NormalZ=1 AngleXU=-3.14159 Radius=1 StartAngle=1.5708 EndAngle=3.14159
    g7: ArcOfCircle CenterX=-56.1991 CenterY=117 CenterZ=0 NormalX=0 NormalY=0 NormalZ=1 AngleXU=-3.14159 Radius=1 StartAngle=0 EndAngle=1.5708
    g8: LineSegment StartX=-57.1991 StartY=140 StartZ=0 EndX=-57.1991 EndY=117 EndZ=0
    g9: LineSegment StartX=-47.1991 StartY=140 StartZ=0 EndX=-57.1991 EndY=140 EndZ=0
    g10: LineSegment StartX=-47.1991 StartY=170 StartZ=0 EndX=-47.1991 EndY=140 EndZ=0
    g11: LineSegment StartX=-47.1991 StartY=170 StartZ=0 EndX=-57.1991 EndY=170 EndZ=0
    g12: LineSegment StartX=-57.1991 StartY=248 StartZ=0 EndX=-57.1991 EndY=170 EndZ=0
    g13: ArcOfCircle CenterX=-56.1991 CenterY=248 CenterZ=0 NormalX=0 NormalY=0 NormalZ=1 AngleXU=-3.14159 Radius=1 StartAngle=4.71239 EndAngle=6.28319
    g14: LineSegment StartX=163.199 StartY=166 StartZ=0 EndX=163.199 EndY=183 EndZ=0
    g15: LineSegment StartX=163.199 StartY=183 StartZ=0 EndX=159.199 EndY=183 EndZ=0
    g16: LineSegment StartX=159.199 StartY=166 StartZ=0 EndX=159.199 EndY=183 EndZ=0
    g17: LineSegment StartX=163.199 StartY=166 StartZ=0 EndX=159.199 EndY=166 EndZ=0
    g18: Circle CenterX=200.199 CenterY=128 CenterZ=0 NormalX=0 NormalY=0 NormalZ=-1 AngleXU=0 Radius=5
    g19: Circle CenterX=-16.1991 CenterY=242 CenterZ=0 NormalX=0 NormalY=0 NormalZ=1 AngleXU=0 Radius=3.5
    g20: Circle CenterX=164.199 CenterY=243 CenterZ=0 NormalX=0 NormalY=0 NormalZ=-1 AngleXU=0 Radius=3.5
    g21: Circle CenterX=147 CenterY=237 CenterZ=0 NormalX=0 NormalY=0 NormalZ=1 AngleXU=0 Radius=2
    g22: Circle CenterX=104 CenterY=237 CenterZ=0 NormalX=0 NormalY=0 NormalZ=1 AngleXU=0 Radius=2
    g23: Circle CenterX=104 CenterY=183 CenterZ=0 NormalX=0 NormalY=0 NormalZ=1 AngleXU=0 Radius=2
    g24: Circle CenterX=147 CenterY=183 CenterZ=0 NormalX=0 NormalY=0 NormalZ=1 AngleXU=0 Radius=2
    g25: Circle CenterX=50 CenterY=214 CenterZ=0 NormalX=0 NormalY=0 NormalZ=1 AngleXU=0 Radius=1.6
    g26: Circle CenterX=5 CenterY=120 CenterZ=0 NormalX=0 NormalY=0 NormalZ=1 AngleXU=0 Radius=1.6
    g27: Circle CenterX=5 CenterY=177 CenterZ=0 NormalX=0 NormalY=0 NormalZ=1 AngleXU=0 Radius=1.6
    g28: Circle CenterX=5 CenterY=183 CenterZ=0 NormalX=0 NormalY=0 NormalZ=1 AngleXU=0 Radius=1.6
    g29: Circle CenterX=5 CenterY=245 CenterZ=0 NormalX=0 NormalY=0 NormalZ=1 AngleXU=0 Radius=1.6
    g30: Circle CenterX=94 CenterY=183 CenterZ=0 NormalX=0 NormalY=0 NormalZ=1 AngleXU=0 Radius=1.6
    g31: Circle CenterX=94 CenterY=120 CenterZ=0 NormalX=0 NormalY=0 NormalZ=1 AngleXU=0 Radius=1.6
    g32: Circle CenterX=94 CenterY=245 CenterZ=0 NormalX=0 NormalY=0 NormalZ=1 AngleXU=0 Radius=1.6
    g33: Circle CenterX=100 CenterY=120 CenterZ=0 NormalX=0 NormalY=0 NormalZ=1 AngleXU=0 Radius=1.6
    g34: Circle CenterX=151 CenterY=172 CenterZ=0 NormalX=0 NormalY=0 NormalZ=1 AngleXU=0 Radius=1.6
    g35: Circle CenterX=100 CenterY=172 CenterZ=0 NormalX=0 NormalY=0 NormalZ=1 AngleXU=0 Radius=1.6
    g36: Circle CenterX=94 CenterY=177 CenterZ=0 NormalX=0 NormalY=0 NormalZ=1 AngleXU=0 Radius=1.6
    g37: Circle CenterX=151 CenterY=120 CenterZ=0 NormalX=0 NormalY=0 NormalZ=1 AngleXU=0 Radius=1.6
    g38: LineSegment StartX=211.199 StartY=249 StartZ=0 EndX=-56.1991 EndY=249 EndZ=0
    g39: LineSegment StartX=-56.1991 StartY=116 StartZ=0 EndX=211.199 EndY=116 EndZ=0
    g40: LineSegment StartX=-1.09956 StartY=249 StartZ=0 EndX=-1.09956 EndY=116 EndZ=0
    g41: LineSegment StartX=156.1 StartY=116 StartZ=0 EndX=156.1 EndY=249 EndZ=0
FEATURE [TechDraw::DrawSVGTemplate] Template001
  EditableTexts = DATE=2021-12-18; DOCUMENT_TYPE=Mechanical assembly drawing; REVISION=REV A; RIGHTS=(R) DO NOT DUPLICATE THIS DRAWING TO THIRD PARTIES WITHOUT OWNER'S PERMISSION !; SCALE=0.5; SIZE=A4; TITLELINE-1=NVM_B1
  Height = 297
  Orientation = 0
  Width = 210
FEATURE [TechDraw::DrawViewPart] View001  label="Flat view"
  CoarseView = false
  Direction = (0,0,1)
  Focus = 100
  HardHidden = false
  IsoCount = 0
  IsoHidden = false
  IsoVisible = false
  LockPosition = false
  Perspective = false
  Rotation = 0
  Scale = 0.5
  ScaleType = 0
  SeamHidden = false
  SeamVisible = true
  SmoothHidden = false
  SmoothVisible = true
  Source = -> [Unfold_Sketch]
  X = 164.017
  XDirection = (0,1,0)
  Y = 144.363
FEATURE [TechDraw::DrawViewDimension] Dimension002
  Arbitrary = false
  ArbitraryTolerances = false
  EqualTolerance = true
  FormatSpec = %.2f
  FormatSpecOverTolerance = %+.2f
  FormatSpecUnderTolerance = %+.2f
  Inverted = false
  LockPosition = false
  MeasureType = 1
  OverTolerance = 0
  References2D = -> [View001]
  Rotation = 0
  ScaleType = 0
  TheoreticalExact = false
  Type = 2
  UnderTolerance = 0
  X = -40.3708
  Y = -0.552582
FEATURE [TechDraw::DrawViewDimension] Dimension003
  Arbitrary = false
  ArbitraryTolerances = false
  EqualTolerance = true
  FormatSpec = %.2f
  FormatSpecOverTolerance = %+.2f
  FormatSpecUnderTolerance = %+.2f
  Inverted = false
  LockPosition = false
  MeasureType = 1
  OverTolerance = 0
  References2D = -> [View001]
  Rotation = 0
  ScaleType = 0
  TheoreticalExact = false
  Type = 1
  UnderTolerance = 0
  X = 1.53846
  Y = 77.6834
FEATURE [TechDraw::DrawSVGTemplate] Template002
  EditableTexts = APPROVER_NAME=APPROVER NAME; AUTHOR_NAME=AUTHOR NAME; DATE=YYYY-MM-DD; DN=DN; DOCUMENT_TYPE=Mechanical assembly drawing; OWNER_NAME=OWNER NAME; PM=PM; PN=PN; REVISION=REV A; RIGHTS=(R) DO NOT DUPLICATE THIS DRAWING TO THIRD PARTIES WITHOUT OWNER'S PERMISSION !; SCALE=M x:x; SHEET=99 of 99; SIZE=A4; TITLELINE-1=FreeCAD; TOLERANCE=+/- ?
  Height = 297
  Orientation = 0
  Width = 210
FEATURE [TechDraw::DrawViewPart] View002
  CoarseView = false
  Direction = (0.577,-0.577,0.577)
  Focus = 100
  HardHidden = false
  IsoCount = 0
  IsoHidden = false
  IsoVisible = false
  LockPosition = false
  Perspective = false
  Rotation = 0
  Scale = 0.5
  ScaleType = 0
  SeamHidden = false
  SeamVisible = true
  SmoothHidden = false
  SmoothVisible = true
  Source = -> [Cut007]
  X = 141.208
  XDirection = (0.71,0.71,0)
  Y = 230.542
FEATURE [TechDraw::DrawViewPart] View003
  CoarseView = false
  Direction = (0,1,0)
  Focus = 100
  HardHidden = false
  IsoCount = 0
  IsoHidden = false
  IsoVisible = false
  LockPosition = false
  Perspective = false
  Rotation = 90
  Scale = 0.5
  ScaleType = 0
  SeamHidden = false
  SeamVisible = true
  SmoothHidden = false
  SmoothVisible = true
  Source = -> [Cut007]
  X = 68.4889
  XDirection = (0,0,1)
  Y = 116.379
FEATURE [TechDraw::DrawViewDimension] Dimension004
  Arbitrary = false
  ArbitraryTolerances = false
  EqualTolerance = true
  FormatSpec = %.2f
  FormatSpecOverTolerance = %+.2f
  FormatSpecUnderTolerance = %+.2f
  Inverted = false
  LockPosition = false
  MeasureType = 1
  OverTolerance = 0
  References2D = -> [View003]
  Rotation = 0
  ScaleType = 0
  TheoreticalExact = false
  Type = 1
  UnderTolerance = 0
  X = -0.875756
  Y = 34.2951
FEATURE [TechDraw::DrawViewDimension] Dimension005
  Arbitrary = false
  ArbitraryTolerances = false
  EqualTolerance = true
  FormatSpec = %.2f
  FormatSpecOverTolerance = %+.2f
  FormatSpecUnderTolerance = %+.2f
  Inverted = false
  LockPosition = false
  MeasureType = 1
  OverTolerance = 0
  References2D = -> [View003]
  Rotation = 0
  ScaleType = 0
  TheoreticalExact = false
  Type = 2
  UnderTolerance = 0
  X = 49.5853
  Y = 0.22207
FEATURE [TechDraw::DrawPage] Page002
  KeepUpdated = true
  NextBalloonIndex = 1
  ProjectionType = 0
  Template = -> Template002
  Views = -> [View002,View003,Dimension004,Dimension005]
FEATURE [TechDraw::DrawViewPart] View004  label="3D_view"
  CoarseView = false
  Direction = (0.577,-0.577,0.577)
  Focus = 100
  HardHidden = false
  IsoCount = 0
  IsoHidden = false
  IsoVisible = false
  LockPosition = false
  Perspective = false
  Rotation = 0
  Scale = 0.5
  ScaleType = 0
  SeamHidden = false
  SeamVisible = true
  SmoothHidden = false
  SmoothVisible = true
  Source = -> [Cut007]
  X = 70.6404
  XDirection = (0.71,0.71,0)
  Y = 244.111
FEATURE [TechDraw::DrawViewPart] View005  label="Side_view"
  CoarseView = false
  Direction = (0,1,0)
  Focus = 100
  HardHidden = false
  IsoCount = 0
  IsoHidden = false
  IsoVisible = false
  LockPosition = false
  Perspective = false
  Rotation = 180
  Scale = 0.5
  ScaleType = 0
  SeamHidden = false
  SeamVisible = true
  SmoothHidden = false
  SmoothVisible = true
  Source = -> [Cut007]
  X = 63.4313
  XDirection = (0.707,0.707,0)
  Y = 87.1811
FEATURE [TechDraw::DrawViewDimension] Dimension006
  Arbitrary = false
  ArbitraryTolerances = false
  EqualTolerance = true
  FormatSpec = %.2f
  FormatSpecOverTolerance = %+.2f
  FormatSpecUnderTolerance = %+.2f
  Inverted = false
  LockPosition = false
  MeasureType = 1
  OverTolerance = 0
  References2D = -> [View005]
  Rotation = 0
  ScaleType = 0
  TheoreticalExact = false
  Type = 1
  UnderTolerance = 0
  X = -1.07037
  Y = 26.1214
FEATURE [TechDraw::DrawViewDimension] Dimension007
  Arbitrary = false
  ArbitraryTolerances = false
  EqualTolerance = true
  FormatSpec = %.2f
  FormatSpecOverTolerance = %+.2f
  FormatSpecUnderTolerance = %+.2f
  Inverted = false
  LockPosition = false
  MeasureType = 1
  OverTolerance = 0
  References2D = -> [View005]
  Rotation = 0
  ScaleType = 0
  TheoreticalExact = false
  Type = 2
  UnderTolerance = 0
  X = 47.6765
  Y = 0.486531
FEATURE [TechDraw::DrawViewDimension] Dimension008
  Arbitrary = false
  ArbitraryTolerances = false
  EqualTolerance = true
  FormatSpec = R%.2f
  FormatSpecOverTolerance = %+.2f
  FormatSpecUnderTolerance = %+.2f
  Inverted = false
  LockPosition = false
  MeasureType = 1
  OverTolerance = 0
  References2D = -> [View005]
  Rotation = 0
  ScaleType = 0
  TheoreticalExact = false
  Type = 4
  UnderTolerance = 0
  X = 48.3168
  Y = -17.3121
FEATURE [TechDraw::DrawViewAnnotation] Annotation  label="Poznamka"
  Font = osifont
  LineSpace = 80
  LockPosition = false
  MaxWidth = -1
  Rotation = 0
  ScaleType = 0
  Text = Material: | 1mm ocelovy plech
  TextSize = 5
  TextStyle = 0
  X = 39.2552
  Y = 166.996
FEATURE [TechDraw::DrawPage] Page001  label="page_B1"
  KeepUpdated = true
  NextBalloonIndex = 1
  ProjectionType = 0
  Template = -> Template001
  Views = -> [View001,Dimension002,Dimension003,View004,View005,Dimension006,Dimension007,Dimension008,Annotation]
FEATURE [Part::Feature] Unfold001
  shape: bbox 294.4 x 106 x 1 mm, 23 faces (baked)
FEATURE [Sketcher::SketchObject] Unfold_Sketch001
  FullyConstrained = false
  sketch-geometry (23):
    g0: ArcOfCircle CenterX=236.199 CenterY=3 CenterZ=0 NormalX=0 NormalY=0 NormalZ=1 AngleXU=-3.14159 Radius=1 StartAngle=1.5708 EndAngle=3.14159
    g1: LineSegment StartX=237.199 StartY=3 StartZ=0 EndX=237.199 EndY=107 EndZ=0
    g2: ArcOfCircle CenterX=236.199 CenterY=107 CenterZ=0 NormalX=0 NormalY=0 NormalZ=1 AngleXU=-3.14159 Radius=1 StartAngle=3.14159 EndAngle=4.71239
    g3: ArcOfCircle CenterX=-56.1991 CenterY=107 CenterZ=0 NormalX=0 NormalY=0 NormalZ=1 AngleXU=-3.14159 Radius=1 StartAngle=4.71239 EndAngle=6.28319
    g4: LineSegment StartX=-57.1991 StartY=107 StartZ=0 EndX=-57.1991 EndY=3 EndZ=0
    g5: ArcOfCircle CenterX=-56.1991 CenterY=3 CenterZ=0 NormalX=0 NormalY=0 NormalZ=1 AngleXU=-3.14159 Radius=1 StartAngle=0 EndAngle=1.5708
    g6: Circle CenterX=-46.1991 CenterY=21 CenterZ=0 NormalX=0 NormalY=0 NormalZ=1 AngleXU=0 Radius=5
    g7: Circle CenterX=226.199 CenterY=14 CenterZ=0 NormalX=0 NormalY=0 NormalZ=-1 AngleXU=0 Radius=5
    g8: Circle CenterX=226.199 CenterY=95 CenterZ=0 NormalX=0 NormalY=0 NormalZ=-1 AngleXU=0 Radius=5
    g9: Circle CenterX=5 CenterY=6 CenterZ=0 NormalX=0 NormalY=0 NormalZ=1 AngleXU=0 Radius=1.6
    g10: Circle CenterX=-37.1991 CenterY=98 CenterZ=0 NormalX=0 NormalY=0 NormalZ=1 AngleXU=0 Radius=1.6
    g11: Circle CenterX=5 CenterY=104 CenterZ=0 NormalX=0 NormalY=0 NormalZ=1 AngleXU=0 Radius=1.6
    g12: Circle CenterX=94 CenterY=6 CenterZ=0 NormalX=0 NormalY=0 NormalZ=1 AngleXU=0 Radius=1.6
    g13: Circle CenterX=100 CenterY=6 CenterZ=0 NormalX=0 NormalY=0 NormalZ=1 AngleXU=0 Radius=1.6
    g14: Circle CenterX=175 CenterY=6 CenterZ=0 NormalX=0 NormalY=0 NormalZ=1 AngleXU=0 Radius=1.6
    g15: Circle CenterX=94 CenterY=104 CenterZ=0 NormalX=0 NormalY=0 NormalZ=1 AngleXU=0 Radius=1.6
    g16: Circle CenterX=100 CenterY=104 CenterZ=0 NormalX=0 NormalY=0 NormalZ=1 AngleXU=0 Radius=1.6
    g17: Circle CenterX=175 CenterY=104 CenterZ=0 NormalX=0 NormalY=0 NormalZ=1 AngleXU=0 Radius=1.6
    g18: Circle CenterX=208.199 CenterY=98 CenterZ=0 NormalX=0 NormalY=0 NormalZ=-1 AngleXU=0 Radius=1.6
    g19: LineSegment StartX=236.199 StartY=108 StartZ=0 EndX=-56.1991 EndY=108 EndZ=0
    g20: LineSegment StartX=-56.1991 StartY=2 StartZ=0 EndX=236.199 EndY=2 EndZ=0
    g21: LineSegment StartX=-1.09956 StartY=108 StartZ=0 EndX=-1.09956 EndY=2 EndZ=0
    g22: LineSegment StartX=181.1 StartY=2 StartZ=0 EndX=181.1 EndY=108 EndZ=0
FEATURE [TechDraw::DrawSVGTemplate] Template003
  EditableTexts = DATE=2021-12-18; DOCUMENT_TYPE=Mechanical assembly drawing; REVISION=REV A; RIGHTS=(R) DO NOT DUPLICATE THIS DRAWING TO THIRD PARTIES WITHOUT OWNER'S PERMISSION !; SCALE=0.5; SIZE=A4; TITLELINE-1=NVM_A1
  Height = 297
  Orientation = 0
  Width = 210
FEATURE [TechDraw::DrawViewPart] View006
  CoarseView = false
  Direction = (0,0,1)
  Focus = 100
  HardHidden = false
  IsoCount = 0
  IsoHidden = false
  IsoVisible = false
  LockPosition = false
  Perspective = false
  Rotation = 0
  Scale = 0.5
  ScaleType = 0
  SeamHidden = false
  SeamVisible = true
  SmoothHidden = false
  SmoothVisible = true
  Source = -> [Unfold_Sketch001]
  X = 162.215
  XDirection = (0,1,0)
  Y = 178.263
FEATURE [TechDraw::DrawViewDimension] Dimension009
  Arbitrary = false
  ArbitraryTolerances = false
  EqualTolerance = true
  FormatSpec = %.2f
  FormatSpecOverTolerance = %+.2f
  FormatSpecUnderTolerance = %+.2f
  Inverted = false
  LockPosition = false
  MeasureType = 1
  OverTolerance = 0
  References2D = -> [View006]
  Rotation = 0
  ScaleType = 0
  TheoreticalExact = false
  Type = 1
  UnderTolerance = 0
  X = -0.111867
  Y = 84.6009
FEATURE [TechDraw::DrawViewDimension] Dimension010
  Arbitrary = false
  ArbitraryTolerances = false
  EqualTolerance = true
  FormatSpec = %.2f
  FormatSpecOverTolerance = %+.2f
  FormatSpecUnderTolerance = %+.2f
  Inverted = false
  LockPosition = false
  MeasureType = 1
  OverTolerance = 0
  References2D = -> [View006]
  Rotation = 0
  ScaleType = 0
  TheoreticalExact = false
  Type = 2
  UnderTolerance = 0
  X = 31.4479
  Y = -1.00887
FEATURE [TechDraw::DrawViewPart] View007
  CoarseView = false
  Direction = (0.577,-0.577,0.577)
  Focus = 100
  HardHidden = false
  IsoCount = 0
  IsoHidden = false
  IsoVisible = false
  LockPosition = false
  Perspective = false
  Rotation = 0
  Scale = 0.5
  ScaleType = 0
  SeamHidden = false
  SeamVisible = true
  SmoothHidden = false
  SmoothVisible = true
  Source = -> [Cut010]
  X = 74.4569
  XDirection = (0.71,0.71,0)
  Y = 234.272
FEATURE [TechDraw::DrawViewPart] View008
  CoarseView = false
  Direction = (0,1,0)
  Focus = 100
  HardHidden = false
  IsoCount = 0
  IsoHidden = false
  IsoVisible = false
  LockPosition = false
  Perspective = false
  Rotation = 180
  Scale = 0.5
  ScaleType = 0
  SeamHidden = false
  SeamVisible = true
  SmoothHidden = false
  SmoothVisible = true
  Source = -> [Cut010]
  X = 69.1415
  XDirection = (1,0,0)
  Y = 98.4197
FEATURE [TechDraw::DrawViewDimension] Dimension011
  Arbitrary = false
  ArbitraryTolerances = false
  EqualTolerance = true
  FormatSpec = %.2f
  FormatSpecOverTolerance = %+.2f
  FormatSpecUnderTolerance = %+.2f
  Inverted = false
  LockPosition = false
  MeasureType = 1
  OverTolerance = 0
  References2D = -> [View008]
  Rotation = 0
  ScaleType = 0
  TheoreticalExact = false
  Type = 1
  UnderTolerance = 0
  X = 0.140121
  Y = 32.1855
FEATURE [TechDraw::DrawViewDimension] Dimension012
  Arbitrary = false
  ArbitraryTolerances = false
  EqualTolerance = true
  FormatSpec = %.2f
  FormatSpecOverTolerance = %+.2f
  FormatSpecUnderTolerance = %+.2f
  Inverted = false
  LockPosition = false
  MeasureType = 1
  OverTolerance = 0
  References2D = -> [View008]
  Rotation = 0
  ScaleType = 0
  TheoreticalExact = false
  Type = 2
  UnderTolerance = 0
  X = 51.8054
  Y = 0.700605
FEATURE [TechDraw::DrawViewAnnotation] Annotation001  label="Poznamka001"
  Font = osifont
  LineSpace = 80
  LockPosition = false
  MaxWidth = -1
  Rotation = 0
  ScaleType = 0
  Text = Material: | 1mm ocelovy plech
  TextSize = 5
  TextStyle = 0
  X = 43.7413
  Y = 164.723
FEATURE [TechDraw::DrawPage] Page003  label="page_A1"
  KeepUpdated = true
  NextBalloonIndex = 1
  ProjectionType = 0
  Template = -> Template003
  Views = -> [View006,Dimension009,Dimension010,View007,View008,Dimension011,Dimension012,Annotation001]
FEATURE [TechDraw::DrawViewAnnotation] Annotation002
  Font = osifont
  LineSpace = 80
  LockPosition = false
  MaxWidth = -1
  Rotation = 0
  ScaleType = 0
  Text = Material: | 2mm Al
  TextSize = 5
  TextStyle = 0
  X = 67.3169
  Y = 90.001
FEATURE [Part::Feature] Unfold002
  shape: bbox 186 x 223.4 x 1 mm, 18 faces (baked)
FEATURE [Sketcher::SketchObject] Unfold_Sketch002
  FullyConstrained = false
  sketch-geometry (18):
    g0: ArcOfCircle CenterX=181 CenterY=164.699 CenterZ=0 NormalX=0 NormalY=0 NormalZ=1 AngleXU=-1.5708 Radius=2 StartAngle=1.5708 EndAngle=3.14159
    g1: LineSegment StartX=181 StartY=166.699 StartZ=0 EndX=-1 EndY=166.699 EndZ=0
    g2: ArcOfCircle CenterX=-1 CenterY=164.699 CenterZ=0 NormalX=0 NormalY=0 NormalZ=1 AngleXU=-1.5708 Radius=2 StartAngle=3.14159 EndAngle=4.71239
    g3: ArcOfCircle CenterX=-1 CenterY=-54.6991 CenterZ=0 NormalX=0 NormalY=0 NormalZ=1 AngleXU=-1.5708 Radius=2 StartAngle=4.71239 EndAngle=6.28319
    g4: LineSegment StartX=-1 StartY=-56.6991 StartZ=0 EndX=181 EndY=-56.6991 EndZ=0
    g5: ArcOfCircle CenterX=181 CenterY=-54.6991 CenterZ=0 NormalX=0 NormalY=0 NormalZ=1 AngleXU=-1.5708 Radius=2 StartAngle=0 EndAngle=1.5708
    g6: Circle CenterX=5 CenterY=6 CenterZ=0 NormalX=0 NormalY=0 NormalZ=1 AngleXU=0 Radius=1.6
    g7: Circle CenterX=5 CenterY=104 CenterZ=0 NormalX=0 NormalY=0 NormalZ=1 AngleXU=0 Radius=1.6
    g8: Circle CenterX=94 CenterY=6 CenterZ=0 NormalX=0 NormalY=0 NormalZ=1 AngleXU=0 Radius=1.6
    g9: Circle CenterX=100 CenterY=6 CenterZ=0 NormalX=0 NormalY=0 NormalZ=1 AngleXU=0 Radius=1.6
    g10: Circle CenterX=175 CenterY=6 CenterZ=0 NormalX=0 NormalY=0 NormalZ=1 AngleXU=0 Radius=1.6
    g11: Circle CenterX=94 CenterY=104 CenterZ=0 NormalX=0 NormalY=0 NormalZ=1 AngleXU=0 Radius=1.6
    g12: Circle CenterX=100 CenterY=104 CenterZ=0 NormalX=0 NormalY=0 NormalZ=1 AngleXU=0 Radius=1.6
    g13: Circle CenterX=175 CenterY=104 CenterZ=0 NormalX=0 NormalY=0 NormalZ=1 AngleXU=0 Radius=1.6
    g14: LineSegment StartX=-3 StartY=164.699 StartZ=0 EndX=-3 EndY=-54.6991 EndZ=0
    g15: LineSegment StartX=183 StartY=-54.6991 StartZ=0 EndX=183 EndY=164.699 EndZ=0
    g16: LineSegment StartX=-3 StartY=1.40044 StartZ=0 EndX=183 EndY=1.40044 EndZ=0
    g17: LineSegment StartX=183 StartY=108.6 StartZ=0 EndX=-3 EndY=108.6 EndZ=0
FEATURE [TechDraw::DrawSVGTemplate] Template004
  EditableTexts = DATE=2021-12-18; DOCUMENT_TYPE=Mechanical assembly drawing; REVISION=REV A; RIGHTS=(R) DO NOT DUPLICATE THIS DRAWING TO THIRD PARTIES WITHOUT OWNER'S PERMISSION !; SCALE=0.5; SIZE=A4; TITLELINE-1=NVM_A2
  Height = 297
  Orientation = 0
  Width = 210
FEATURE [TechDraw::DrawViewPart] View009
  CoarseView = false
  Direction = (0,0,1)
  Focus = 100
  HardHidden = false
  IsoCount = 0
  IsoHidden = false
  IsoVisible = false
  LockPosition = false
  Perspective = false
  Rotation = 0
  Scale = 0.5
  ScaleType = 0
  SeamHidden = false
  SeamVisible = true
  SmoothHidden = false
  SmoothVisible = true
  Source = -> [Unfold_Sketch002]
  X = 132.5
  XDirection = (1,0,0)
  Y = 221.833
FEATURE [TechDraw::DrawViewPart] View010
  CoarseView = false
  Direction = (0.577,-0.577,0.577)
  Focus = 100
  HardHidden = false
  IsoCount = 0
  IsoHidden = false
  IsoVisible = false
  LockPosition = false
  Perspective = false
  Rotation = 0
  Scale = 0.5
  ScaleType = 0
  SeamHidden = false
  SeamVisible = true
  SmoothHidden = false
  SmoothVisible = true
  Source = -> [Cut009]
  X = 70.1667
  XDirection = (0.707,0.707,0)
  Y = 97.625
FEATURE [TechDraw::DrawViewPart] View011
  CoarseView = false
  Direction = (1,0,0)
  Focus = 100
  HardHidden = false
  IsoCount = 0
  IsoHidden = false
  IsoVisible = false
  LockPosition = false
  Perspective = false
  Rotation = 0
  Scale = 0.5
  ScaleType = 0
  SeamHidden = false
  SeamVisible = true
  SmoothHidden = false
  SmoothVisible = true
  Source = -> [Cut009]
  X = 164.125
  XDirection = (0.707,0.707,0)
  Y = 91.2083
FEATURE [TechDraw::DrawViewDimension] Dimension013
  Arbitrary = false
  ArbitraryTolerances = false
  EqualTolerance = true
  FormatSpec = %.2f
  FormatSpecOverTolerance = %+.2f
  FormatSpecUnderTolerance = %+.2f
  Inverted = false
  LockPosition = false
  MeasureType = 1
  OverTolerance = 0
  References2D = -> [View009]
  Rotation = 0
  ScaleType = 0
  TheoreticalExact = false
  Type = 1
  UnderTolerance = 0
  X = -0.389225
  Y = 66.2344
FEATURE [TechDraw::DrawViewDimension] Dimension014
  Arbitrary = false
  ArbitraryTolerances = false
  EqualTolerance = true
  FormatSpec = %.2f
  FormatSpecOverTolerance = %+.2f
  FormatSpecUnderTolerance = %+.2f
  Inverted = false
  LockPosition = false
  MeasureType = 1
  OverTolerance = 0
  References2D = -> [View009]
  Rotation = 0
  ScaleType = 0
  TheoreticalExact = false
  Type = 2
  UnderTolerance = 0
  X = 54.2576
  Y = -1.16768
FEATURE [TechDraw::DrawViewDimension] Dimension015
  Arbitrary = false
  ArbitraryTolerances = false
  EqualTolerance = true
  FormatSpec = %.2f
  FormatSpecOverTolerance = %+.2f
  FormatSpecUnderTolerance = %+.2f
  Inverted = false
  LockPosition = false
  MeasureType = 1
  OverTolerance = 0
  References2D = -> [View011]
  Rotation = 0
  ScaleType = 0
  TheoreticalExact = false
  Type = 1
  UnderTolerance = 0
  X = -2.09733
  Y = 28.8014
FEATURE [TechDraw::DrawViewDimension] Dimension016
  Arbitrary = false
  ArbitraryTolerances = false
  EqualTolerance = true
  FormatSpec = %.2f
  FormatSpecOverTolerance = %+.2f
  FormatSpecUnderTolerance = %+.2f
  Inverted = false
  LockPosition = false
  MeasureType = 1
  OverTolerance = 0
  References2D = -> [View011]
  Rotation = 0
  ScaleType = 0
  TheoreticalExact = false
  Type = 2
  UnderTolerance = 0
  X = 31.5926
  Y = -0.403549
FEATURE [Part::Feature] Unfold003
  shape: bbox 161 x 250.4 x 1 mm, 27 faces (baked)
FEATURE [Sketcher::SketchObject] Unfold_Sketch003
  FullyConstrained = false
  sketch-geometry (27):
    g0: ArcOfCircle CenterX=156 CenterY=305.699 CenterZ=0 NormalX=0 NormalY=0 NormalZ=1 AngleXU=-1.5708 Radius=2 StartAngle=1.5708 EndAngle=3.14159
    g1: LineSegment StartX=156 StartY=307.699 StartZ=0 EndX=-1 EndY=307.699 EndZ=0
    g2: ArcOfCircle CenterX=-1 CenterY=305.699 CenterZ=0 NormalX=0 NormalY=0 NormalZ=1 AngleXU=-1.5708 Radius=2 StartAngle=3.14159 EndAngle=4.71239
    g3: ArcOfCircle CenterX=-1 CenterY=59.3009 CenterZ=0 NormalX=0 NormalY=0 NormalZ=1 AngleXU=-1.5708 Radius=2 StartAngle=4.71239 EndAngle=6.28319
    g4: LineSegment StartX=-1 StartY=57.3009 StartZ=0 EndX=156 EndY=57.3009 EndZ=0
    g5: ArcOfCircle CenterX=156 CenterY=59.3009 CenterZ=0 NormalX=0 NormalY=0 NormalZ=1 AngleXU=-1.5708 Radius=2 StartAngle=0 EndAngle=1.5708
    g6: Circle CenterX=8 CenterY=296.699 CenterZ=0 NormalX=0 NormalY=0 NormalZ=-1 AngleXU=-3.14159 Radius=1.6
    g7: Circle CenterX=8 CenterY=260.699 CenterZ=0 NormalX=0 NormalY=0 NormalZ=-1 AngleXU=-3.14159 Radius=1.6
    g8: Circle CenterX=147 CenterY=296.699 CenterZ=0 NormalX=0 NormalY=0 NormalZ=-1 AngleXU=-3.14159 Radius=1.6
    g9: Circle CenterX=147 CenterY=260.699 CenterZ=0 NormalX=0 NormalY=0 NormalZ=-1 AngleXU=-3.14159 Radius=1.6
    g10: Circle CenterX=50 CenterY=214 CenterZ=0 NormalX=0 NormalY=0 NormalZ=1 AngleXU=0 Radius=1.6
    g11: Circle CenterX=5 CenterY=183 CenterZ=0 NormalX=0 NormalY=0 NormalZ=1 AngleXU=0 Radius=1.6
    g12: Circle CenterX=5 CenterY=245 CenterZ=0 NormalX=0 NormalY=0 NormalZ=1 AngleXU=0 Radius=1.6
    g13: Circle CenterX=5 CenterY=177 CenterZ=0 NormalX=0 NormalY=0 NormalZ=1 AngleXU=0 Radius=1.6
    g14: Circle CenterX=5 CenterY=120 CenterZ=0 NormalX=0 NormalY=0 NormalZ=1 AngleXU=0 Radius=1.6
    g15: Circle CenterX=151 CenterY=172 CenterZ=0 NormalX=0 NormalY=0 NormalZ=1 AngleXU=0 Radius=1.6
    g16: Circle CenterX=100 CenterY=172 CenterZ=0 NormalX=0 NormalY=0 NormalZ=1 AngleXU=0 Radius=1.6
    g17: Circle CenterX=94 CenterY=177 CenterZ=0 NormalX=0 NormalY=0 NormalZ=1 AngleXU=0 Radius=1.6
    g18: Circle CenterX=151 CenterY=120 CenterZ=0 NormalX=0 NormalY=0 NormalZ=1 AngleXU=0 Radius=1.6
    g19: Circle CenterX=94 CenterY=183 CenterZ=0 NormalX=0 NormalY=0 NormalZ=1 AngleXU=0 Radius=1.6
    g20: Circle CenterX=94 CenterY=245 CenterZ=0 NormalX=0 NormalY=0 NormalZ=1 AngleXU=0 Radius=1.6
    g21: Circle CenterX=100 CenterY=120 CenterZ=0 NormalX=0 NormalY=0 NormalZ=1 AngleXU=0 Radius=1.6
    g22: Circle CenterX=94 CenterY=120 CenterZ=0 NormalX=0 NormalY=0 NormalZ=1 AngleXU=0 Radius=1.6
    g23: LineSegment StartX=-3 StartY=305.699 StartZ=0 EndX=-3 EndY=59.3009 EndZ=0
    g24: LineSegment StartX=158 StartY=59.3009 StartZ=0 EndX=158 EndY=305.699 EndZ=0
    g25: LineSegment StartX=-3 StartY=115.4 StartZ=0 EndX=158 EndY=115.4 EndZ=0
    g26: LineSegment StartX=158 StartY=249.6 StartZ=0 EndX=-3 EndY=249.6 EndZ=0
FEATURE [TechDraw::DrawSVGTemplate] Template005
  EditableTexts = DATE=2021-12-18; DOCUMENT_TYPE=Mechanical assembly drawing; REVISION=REV A; RIGHTS=(R) DO NOT DUPLICATE THIS DRAWING TO THIRD PARTIES WITHOUT OWNER'S PERMISSION !; SCALE=0.5; SIZE=A4; TITLELINE-1=NVM_B2
  Height = 297
  Orientation = 0
  Width = 210
FEATURE [TechDraw::DrawViewPart] View012
  CoarseView = false
  Direction = (0,0,1)
  Focus = 100
  HardHidden = false
  IsoCount = 0
  IsoHidden = false
  IsoVisible = false
  LockPosition = false
  Perspective = false
  Rotation = 0
  Scale = 0.5
  ScaleType = 0
  SeamHidden = false
  SeamVisible = true
  SmoothHidden = false
  SmoothVisible = true
  Source = -> [Unfold_Sketch003]
  X = 150.337
  XDirection = (1,0,0)
  Y = 215.659
FEATURE [TechDraw::DrawViewPart] View013
  CoarseView = false
  Direction = (0.577,-0.577,0.577)
  Focus = 100
  HardHidden = false
  IsoCount = 0
  IsoHidden = false
  IsoVisible = false
  LockPosition = false
  Perspective = false
  Rotation = 0
  Scale = 0.5
  ScaleType = 0
  SeamHidden = false
  SeamVisible = true
  SmoothHidden = false
  SmoothVisible = true
  Source = -> [Cut011]
  X = 70.1667
  XDirection = (0.707,0.707,0)
  Y = 119.509
FEATURE [TechDraw::DrawViewPart] View014
  CoarseView = false
  Direction = (1,0,0)
  Focus = 100
  HardHidden = false
  IsoCount = 0
  IsoHidden = false
  IsoVisible = false
  LockPosition = false
  Perspective = false
  Rotation = 180
  Scale = 0.5
  ScaleType = 0
  SeamHidden = false
  SeamVisible = true
  SmoothHidden = false
  SmoothVisible = true
  Source = -> [Cut011]
  X = 156.238
  XDirection = (0.707,0.707,0)
  Y = 72.5849
FEATURE [TechDraw::DrawViewDimension] Dimension017
  Arbitrary = false
  ArbitraryTolerances = false
  EqualTolerance = true
  FormatSpec = %.2f
  FormatSpecOverTolerance = %+.2f
  FormatSpecUnderTolerance = %+.2f
  Inverted = false
  LockPosition = false
  MeasureType = 1
  OverTolerance = 0
  References2D = -> [View014]
  Rotation = 0
  ScaleType = 0
  TheoreticalExact = false
  Type = 2
  UnderTolerance = 0
  X = -48.3392
  Y = -0.729797
FEATURE [TechDraw::DrawViewDimension] Dimension018
  Arbitrary = false
  ArbitraryTolerances = false
  EqualTolerance = true
  FormatSpec = %.2f
  FormatSpecOverTolerance = %+.2f
  FormatSpecUnderTolerance = %+.2f
  Inverted = false
  LockPosition = false
  MeasureType = 1
  OverTolerance = 0
  References2D = -> [View014]
  Rotation = 0
  ScaleType = 0
  TheoreticalExact = false
  Type = 1
  UnderTolerance = 0
  X = -0.473017
  Y = 25.3591
FEATURE [TechDraw::DrawViewDimension] Dimension019
  Arbitrary = false
  ArbitraryTolerances = false
  EqualTolerance = true
  FormatSpec = %.2f
  FormatSpecOverTolerance = %+.2f
  FormatSpecUnderTolerance = %+.2f
  Inverted = false
  LockPosition = false
  MeasureType = 1
  OverTolerance = 0
  References2D = -> [View012]
  Rotation = 0
  ScaleType = 0
  TheoreticalExact = false
  Type = 2
  UnderTolerance = 0
  X = 44.7758
  Y = 0.184194
FEATURE [TechDraw::DrawViewDimension] Dimension020
  Arbitrary = false
  ArbitraryTolerances = false
  EqualTolerance = true
  FormatSpec = %.2f
  FormatSpecOverTolerance = %+.2f
  FormatSpecUnderTolerance = %+.2f
  Inverted = false
  LockPosition = false
  MeasureType = 1
  OverTolerance = 0
  References2D = -> [View012]
  Rotation = 0
  ScaleType = 0
  TheoreticalExact = false
  Type = 1
  UnderTolerance = 0
  X = 0.097306
  Y = 71.5248
FEATURE [TechDraw::DrawViewAnnotation] Annotation003
  Font = osifont
  LineSpace = 80
  LockPosition = false
  MaxWidth = -1
  Rotation = 0
  ScaleType = 0
  Text = Material: | 1mm ocelovy plech
  TextSize = 5
  TextStyle = 0
  X = 50
  Y = 241.083
FEATURE [TechDraw::DrawPage] Page005
  KeepUpdated = true
  NextBalloonIndex = 1
  ProjectionType = 0
  Template = -> Template005
  Views = -> [View012,View013,View014,Dimension017,Dimension018,Dimension019,Dimension020,Annotation003]
FEATURE [TechDraw::DrawViewAnnotation] Annotation004
  Font = osifont
  LineSpace = 80
  LockPosition = false
  MaxWidth = -1
  Rotation = 0
  ScaleType = 0
  Text = Material: | 1mm ocelovy plech
  TextSize = 5
  TextStyle = 0
  X = 42.6667
  Y = 228.708
FEATURE [TechDraw::DrawPage] Page004
  KeepUpdated = true
  NextBalloonIndex = 1
  ProjectionType = 0
  Template = -> Template004
  Views = -> [View009,View010,View011,Dimension013,Dimension014,Dimension015,Dimension016,Annotation004]
FEATURE [TechDraw::DrawSVGTemplate] Template006
  Height = 297
  Orientation = 0
  Width = 210
FEATURE [TechDraw::DrawViewPart] View015
  CoarseView = false
  Direction = (0.577,-0.577,0.577)
  Focus = 100
  HardHidden = false
  IsoCount = 0
  IsoHidden = false
  IsoVisible = false
  LockPosition = false
  Perspective = false
  Rotation = 0
  Scale = 0.75
  ScaleType = 0
  SeamHidden = false
  SeamVisible = true
  SmoothHidden = false
  SmoothVisible = true
  Source = -> [Cut009,Cut010]
  X = 105
  XDirection = (0.707,0.707,0)
  Y = 148.5
FEATURE [TechDraw::DrawPage] Page006
  KeepUpdated = true
  NextBalloonIndex = 1
  ProjectionType = 0
  Template = -> Template006
  Views = -> [View015]
FEATURE [TechDraw::DrawSVGTemplate] Template007
  Height = 297
  Orientation = 0
  Width = 210
FEATURE [TechDraw::DrawViewPart] View016
  CoarseView = false
  Direction = (0.577,-0.577,0.577)
  Focus = 100
  HardHidden = false
  IsoCount = 0
  IsoHidden = false
  IsoVisible = false
  LockPosition = false
  Perspective = false
  Rotation = 0
  Scale = 0.75
  ScaleType = 0
  SeamHidden = false
  SeamVisible = true
  SmoothHidden = false
  SmoothVisible = true
  Source = -> [Cut007,Cut011]
  X = 105
  XDirection = (0.71,0.71,0)
  Y = 148.5
FEATURE [TechDraw::DrawPage] Page007
  KeepUpdated = true
  NextBalloonIndex = 1
  ProjectionType = 0
  Template = -> Template007
  Views = -> [View016]
FEATURE [TechDraw::DrawViewDimension] Dimension021
  Arbitrary = false
  ArbitraryTolerances = false
  EqualTolerance = true
  FormatSpec = %.2f
  FormatSpecOverTolerance = %+.2f
  FormatSpecUnderTolerance = %+.2f
  Inverted = false
  LockPosition = false
  MeasureType = 1
  OverTolerance = 0
  References2D = -> [View]
  Rotation = 0
  ScaleType = 0
  TheoreticalExact = false
  Type = 1
  UnderTolerance = 0
  X = -19.0499
  Y = 69.1557
FEATURE [TechDraw::DrawViewDimension] Dimension022
  Arbitrary = false
  ArbitraryTolerances = false
  EqualTolerance = true
  FormatSpec = %.2f
  FormatSpecOverTolerance = %+.2f
  FormatSpecUnderTolerance = %+.2f
  Inverted = false
  LockPosition = false
  MeasureType = 1
  OverTolerance = 0
  References2D = -> [View]
  Rotation = 0
  ScaleType = 0
  TheoreticalExact = false
  Type = 2
  UnderTolerance = 0
  X = -50.4548
  Y = 44.0506
FEATURE [TechDraw::DrawViewDimension] Dimension023
  Arbitrary = false
  ArbitraryTolerances = false
  EqualTolerance = true
  FormatSpec = %.2f
  FormatSpecOverTolerance = %+.2f
  FormatSpecUnderTolerance = %+.2f
  Inverted = false
  LockPosition = false
  MeasureType = 1
  OverTolerance = 0
  References2D = -> [View]
  Rotation = 0
  ScaleType = 0
  TheoreticalExact = false
  Type = 1
  UnderTolerance = 0
  X = -30.2
  Y = 50.75
FEATURE [TechDraw::DrawViewDimension] Dimension024
  Arbitrary = false
  ArbitraryTolerances = false
  EqualTolerance = true
  FormatSpec = %.2f
  FormatSpecOverTolerance = %+.2f
  FormatSpecUnderTolerance = %+.2f
  Inverted = false
  LockPosition = false
  MeasureType = 1
  OverTolerance = 0
  References2D = -> [View]
  Rotation = 0
  ScaleType = 0
  TheoreticalExact = false
  Type = 2
  UnderTolerance = 0
  X = -15.192
  Y = 50.4498
FEATURE [TechDraw::DrawViewDimension] Dimension025
  Arbitrary = false
  ArbitraryTolerances = false
  EqualTolerance = true
  FormatSpec = %.2f
  FormatSpecOverTolerance = %+.2f
  FormatSpecUnderTolerance = %+.2f
  Inverted = false
  LockPosition = false
  MeasureType = 1
  OverTolerance = 0
  References2D = -> [View]
  Rotation = 0
  ScaleType = 0
  TheoreticalExact = false
  Type = 1
  UnderTolerance = 0
  X = -19.2
  Y = 24.5
FEATURE [TechDraw::DrawViewDimension] Dimension026
  Arbitrary = false
  ArbitraryTolerances = false
  EqualTolerance = true
  FormatSpec = %.2f
  FormatSpecOverTolerance = %+.2f
  FormatSpecUnderTolerance = %+.2f
  Inverted = false
  LockPosition = false
  MeasureType = 1
  OverTolerance = 0
  References2D = -> [View]
  Rotation = 0
  ScaleType = 0
  TheoreticalExact = false
  Type = 2
  UnderTolerance = 0
  X = -49.3414
  Y = 10.0527
FEATURE [TechDraw::DrawViewDimension] Dimension027
  Arbitrary = false
  ArbitraryTolerances = false
  EqualTolerance = true
  FormatSpec = %.2f
  FormatSpecOverTolerance = %+.2f
  FormatSpecUnderTolerance = %+.2f
  Inverted = false
  LockPosition = false
  MeasureType = 1
  OverTolerance = 0
  References2D = -> [View]
  Rotation = 0
  ScaleType = 0
  TheoreticalExact = false
  Type = 1
  UnderTolerance = 0
  X = 18.8
  Y = 22
FEATURE [TechDraw::DrawViewDimension] Dimension028
  Arbitrary = false
  ArbitraryTolerances = false
  EqualTolerance = true
  FormatSpec = %.2f
  FormatSpecOverTolerance = %+.2f
  FormatSpecUnderTolerance = %+.2f
  Inverted = false
  LockPosition = false
  MeasureType = 1
  OverTolerance = 0
  References2D = -> [View]
  Rotation = 0
  ScaleType = 0
  TheoreticalExact = false
  Type = 2
  UnderTolerance = 0
  X = 35.693
  Y = 8.21086
FEATURE [TechDraw::DrawViewDimension] Dimension029
  Arbitrary = false
  ArbitraryTolerances = false
  EqualTolerance = true
  FormatSpec = %.2f
  FormatSpecOverTolerance = %+.2f
  FormatSpecUnderTolerance = %+.2f
  Inverted = false
  LockPosition = false
  MeasureType = 1
  OverTolerance = 0
  References2D = -> [View]
  Rotation = 0
  ScaleType = 0
  TheoreticalExact = false
  Type = 2
  UnderTolerance = 0
  X = -49.0126
  Y = -37.322
FEATURE [TechDraw::DrawViewDimension] Dimension030
  Arbitrary = false
  ArbitraryTolerances = false
  EqualTolerance = true
  FormatSpec = %.2f
  FormatSpecOverTolerance = %+.2f
  FormatSpecUnderTolerance = %+.2f
  Inverted = false
  LockPosition = false
  MeasureType = 1
  OverTolerance = 0
  References2D = -> [View]
  Rotation = 0
  ScaleType = 0
  TheoreticalExact = false
  Type = 1
  UnderTolerance = 0
  X = -19.2
  Y = -12
FEATURE [TechDraw::DrawViewDimension] Dimension031
  Arbitrary = false
  ArbitraryTolerances = false
  EqualTolerance = true
  FormatSpec = %.2f
  FormatSpecOverTolerance = %+.2f
  FormatSpecUnderTolerance = %+.2f
  Inverted = false
  LockPosition = false
  MeasureType = 1
  OverTolerance = 0
  References2D = -> [View]
  Rotation = 0
  ScaleType = 0
  TheoreticalExact = false
  Type = 1
  UnderTolerance = 0
  X = 4.7144
  Y = -24.8235
FEATURE [TechDraw::DrawViewDimension] Dimension032
  Arbitrary = false
  ArbitraryTolerances = false
  EqualTolerance = true
  FormatSpec = %.2f
  FormatSpecOverTolerance = %+.2f
  FormatSpecUnderTolerance = %+.2f
  Inverted = false
  LockPosition = false
  MeasureType = 1
  OverTolerance = 0
  References2D = -> [View]
  Rotation = 0
  ScaleType = 0
  TheoreticalExact = false
  Type = 1
  UnderTolerance = 0
  X = 24.8
  Y = -12
FEATURE [TechDraw::DrawPage] Page  label="page_base"
  KeepUpdated = true
  NextBalloonIndex = 1
  ProjectionType = 0
  Template = -> Template
  Views = -> [View,Dimension,Dimension001,Annotation002,Dimension021,Dimension022,Dimension023,Dimension024,Dimension025,Dimension026,Dimension027,Dimension028,Dimension029,Dimension030,Dimension031,Dimension032]
